# Revit family: Circular_Wash_Fountain-Six_Station-Acorn-3506DBS_Series
name_source: partatom
category: Plumbing Fixtures
units: mm (PartAtom-declared; Revit-internal decimal feet)

## family parameters
Cut with Voids When Loaded = No
Host = Face
OmniClass Number = 23.45.05.14.14
OmniClass Title = Sinks/Lavatories
Part Type = Normal
Room Calculation Point = No
Round Connector Dimension = Use Diameter
Shared = Yes

## types (2) — shared parameters
3 On-Floor, Floor Outlet = Yes
Assembly Code = D2010600
BO - Bottom Supply; Vent Off-Drain = No
BT - Bottom Supply; Vent Thru-Fixture = No
Base Material = Galvanized Steel-Acorn-Black Vinylclad
Bowl Depth = 9"
CW Connection = Yes
CWFU = 2
DP- Metering Powder Soap Dispenser = No
DV- Liquid/ Lotion Soap Dispenser = No
Default Elevation = 0"
Description = Six Station, 9 in. Deep Bowl, Circular Wash Fountain
Diameter = 38 1/4"
EG - Enviro-Glaze Color, Bowl and Sprayhead (Specify) = No
Finish = Stainless Steel-Acorn-Satin
Flow Rate = 0.5 GPM
H- Hand Operation = Yes
HB- Hose Bibb, Specify; Left or Right = No
HW Connection = Yes
HWFU = 2
Height = 44"
Inlet Connection Diameter = 1/2"
Installation Instruction Link = https://www.acorneng.com
Installation Type = Floor Mounted
JH31 - 31" Junior Rim Height = No
Manufacturer = Acorn Engineering
Material = Stainless Steel-Acorn-Satin
Minimum Operating Pressure = A minimum of 30 PSI supply pressure is required
PCB Pipe Column Brace (Pipe By Others) = No
PDM Metering Liquid Soap Dispenser = No
PPZ Programmable Piezo Pushbutton Electronic Metering = No
Product Documentation Link = https://www.acorneng.com
Product Page URL = https://www.acorneng.com
SC - Supply Cover, Ceiling Height_______ = No
SO - Sensor Operation = No
SO-BAT- Sensor Operation (Batteries Not Included) = No
SPX- 16 Gage Stainless Steel Housing = No
ST- Single Temperature Valve = No
TM- C or Multi-Fold Paper Towel Dispenser = No
TO - Top Supply; Vent Off Drain = No
TS- Single-Fold Paper Towel Dispenser = No
TT - Top Supply; Vent Thru-Fixture = No
URL = http://www.acorneng.com
Vent Connection = No
WFU = 3
Waste Connection = Yes
Waste Connection Diameter = 2"
Waste Outlet Height (Dim A) = 16 1/2"

## per-type parameters (varying)
| type | Dimension A | Dimension B | F - Foot Operation | Type Comments |
| 3506-DBS-3-H | 19 1/4" | 20 1/2" | No | Island Circular, Six Station |
| 3506-DBS-3-H-F | 23 1/4" | 34 3/8" | Yes | Island Circular, Six Station, Foot Operation |

note: column(s) folded — value = type name in every type: Model

## geometry (parser evidence)
native form markers: Sweep x2
no freeform markers — native parametric forms only
